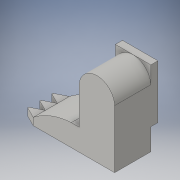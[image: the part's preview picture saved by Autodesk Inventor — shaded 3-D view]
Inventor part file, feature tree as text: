
AUTODESK INVENTOR PART (.ipt)
format: ipt  version: 2016 (Build 200138000, 138)  size: 158,208 bytes
history: native  units: in
note: dims shown in document units (in); Inventor stores cm internally (conversion verified against a paired STEP export)
features: sketch x9, other x3, plane x1
ambient origin geometry x8: Origin, YZ Plane, XZ Plane, XY Plane, X Axis, Y Axis, Z Axis, Center Point
bodies: Solid1 (feature_tree)
feature tree (13):
  other  "Leg.ipt"
  other  "Solid1::Leg.ipt"
  other  "TaggingFeature1"
  sketch  "Sketch1"  dims[d0=0.3937in]
  sketch  "Sketch2"
  sketch  "Sketch3"
  sketch  "Sketch5"
  sketch  "Sketch6"
  sketch  "Sketch7"
  sketch  "Sketch8"
  sketch  "Sketch9"
  sketch  "Sketch10"
  plane  "Work Plane1"
